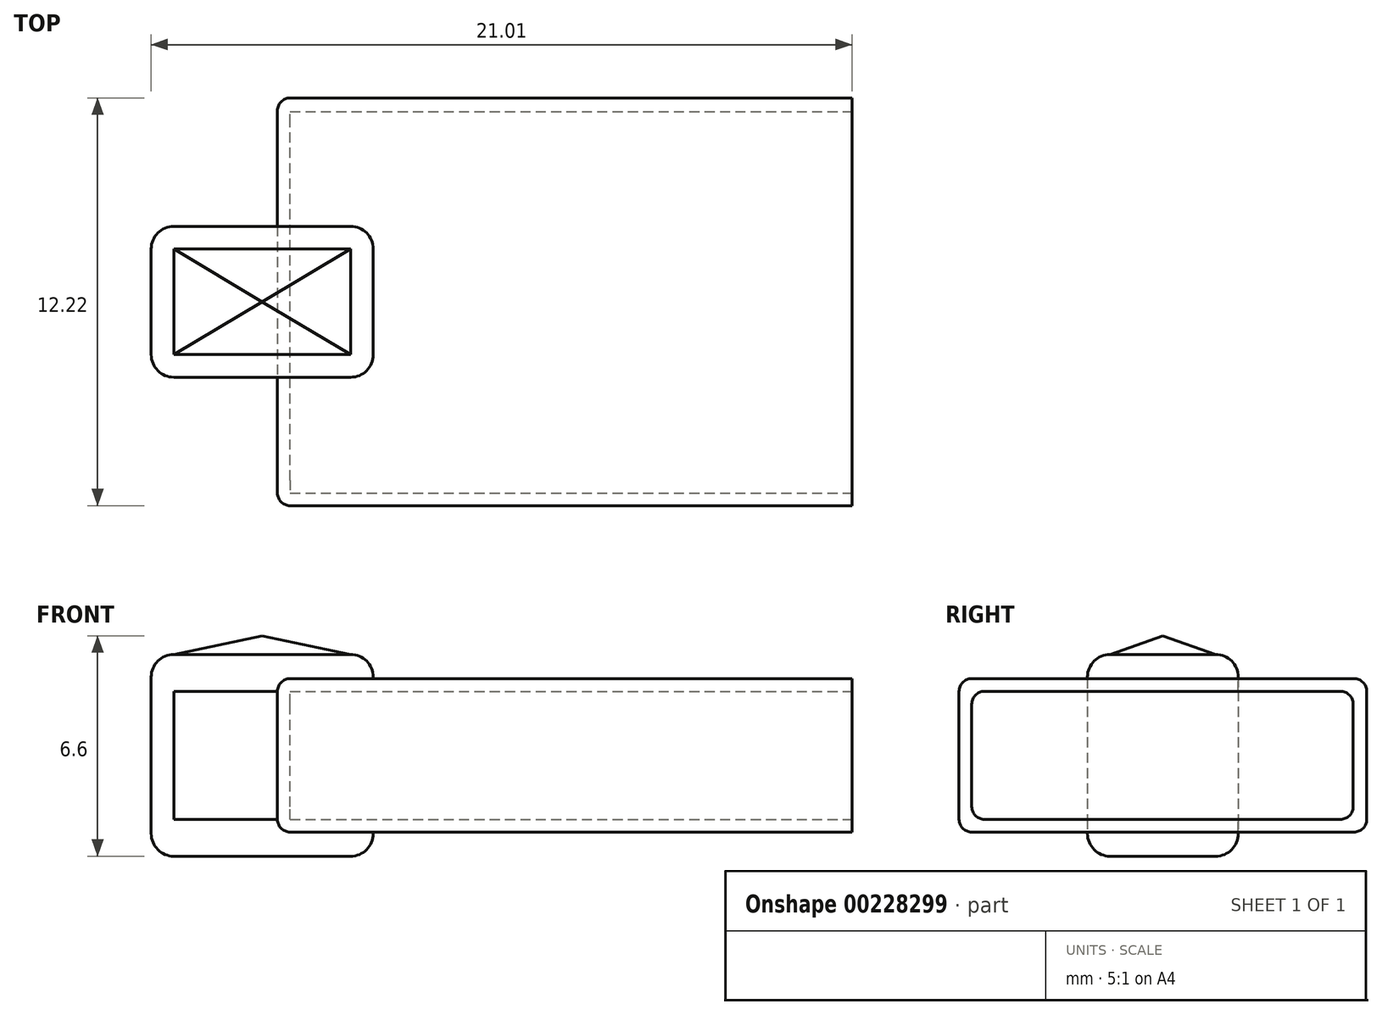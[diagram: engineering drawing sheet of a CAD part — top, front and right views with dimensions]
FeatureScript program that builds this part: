
annotation { "Feature Type Name" : "Feature", "Feature Type Description" : "" }
export const myFeature = defineFeature(function(context is Context, id is Id, definition is map)
    precondition{}
    {
        {
            var Q0;
            Q0=qCreatedBy(makeId("Top.planeOp"),FACE);
            var sketch = newSketch(context, id + "F0", { "sketchPlane" : qUnion([Q0])});
            skLineSegment(sketch, "E0", {"start": v(-8.61, -6.1) * mm, "end": v(-8.61, 6.1) * mm});
            skLineSegment(sketch, "E1", {"start": v(-8.61, 6.1) * mm, "end": v(8.61, 6.1) * mm});
            skLineSegment(sketch, "E2", {"start": v(8.61, 6.1) * mm, "end": v(8.61, -6.1) * mm});
            skLineSegment(sketch, "E3", {"start": v(8.61, -6.1) * mm, "end": v(-8.61, -6.1) * mm});
            skSolve(sketch);
        }
        {
            var Q0;
            Q0=qCreatedBy(makeId("Top.planeOp"),FACE);
            var sketch = newSketch(context, id + "F1", { "sketchPlane" : qUnion([Q0])});
            skLineSegment(sketch, "E4", {"start": v(-12.4, 2.26) * mm, "end": v(-5.74, 2.26) * mm});
            skLineSegment(sketch, "E5", {"start": v(-5.74, 2.26) * mm, "end": v(-5.74, -2.26) * mm});
            skLineSegment(sketch, "E6", {"start": v(-5.74, -2.26) * mm, "end": v(-12.4, -2.26) * mm});
            skLineSegment(sketch, "E7", {"start": v(-12.4, -2.26) * mm, "end": v(-12.4, 2.26) * mm});
            skSolve(sketch);
        }
        {
            var Q0;
            Q0 = qSketchRegion(id + "F0", true);
            extrude(context, id + "F2", {"entities" : qUnion([Q0]), "endBound" : BoundingType.SYMMETRIC, "depth" : 4.6 * mm});
        }
        {
            var Q0;
            Q0=makeQuery(id+"F1.imprint","IMPRINT",FACE,{"disambiguationData":[TD([[makeQuery(id+"F1.imprint","IMPRINT",EDGE,{"derivedFrom":sQuery(id+"F1.wireOp",EDGE,"E4")}),-1.0]])]});
            extrude(context, id + "F3", {"entities" : qUnion([Q0]), "operationType" : NewBodyOperationType.ADD, "endBound" : BoundingType.SYMMETRIC, "depth" : 6.05 * mm});
        }
        {
            var Q0;
            Q0=makeQuery(id+"F3.opExtrude","CAP_EDGE",EDGE,{"disambiguationData":[OSD([sQuery(id+"F1.wireOp",EDGE,"E4")])],"isStart":false});
            var Q1;
            Q1=makeQuery(id+"F3.opExtrude","CAP_EDGE",EDGE,{"disambiguationData":[OSD([sQuery(id+"F1.wireOp",EDGE,"E4")])],"isStart":true});
            var Q2;
            Q2=makeQuery(id+"F3.opExtrude","CAP_EDGE",EDGE,{"disambiguationData":[OSD([sQuery(id+"F1.wireOp",EDGE,"E6")])],"isStart":false});
            var Q3;
            Q3=makeQuery(id+"F3.opExtrude","CAP_EDGE",EDGE,{"disambiguationData":[OSD([sQuery(id+"F1.wireOp",EDGE,"E6")])],"isStart":true});
            var Q4;
            Q4=makeQuery(id+"F3.opExtrude","CAP_EDGE",EDGE,{"disambiguationData":[OSD([sQuery(id+"F1.wireOp",EDGE,"E5")])],"isStart":true});
            var Q5;
            Q5=makeQuery(id+"F3.opExtrude","CAP_EDGE",EDGE,{"disambiguationData":[OSD([sQuery(id+"F1.wireOp",EDGE,"E5")])],"isStart":false});
            var Q6;
            Q6=makeQuery(id+"F3.opExtrude","SWEPT_EDGE",EDGE,{"disambiguationData":[OSD([sQuery(id+"F1.wireOp",EDGE,"E6"),sQuery(id+"F1.wireOp",EDGE,"E7")])]});
            var Q7;
            Q7=makeQuery(id+"F3.opExtrude","SWEPT_EDGE",EDGE,{"disambiguationData":[OSD([sQuery(id+"F1.wireOp",EDGE,"E4"),sQuery(id+"F1.wireOp",EDGE,"E7")])]});
            var Q8;
            Q8=makeQuery(id+"F3.opExtrude","CAP_EDGE",EDGE,{"disambiguationData":[OSD([sQuery(id+"F1.wireOp",EDGE,"E7")])],"isStart":true});
            var Q9;
            Q9=makeQuery(id+"F3.opExtrude","CAP_EDGE",EDGE,{"disambiguationData":[OSD([sQuery(id+"F1.wireOp",EDGE,"E7")])],"isStart":false});
            var Q10;
            {var subQ0=sQuery(id+"F1.wireOp",EDGE,"E4");var subQ1=sQuery(id+"F1.wireOp",EDGE,"E5");Q10=makeQuery(id+"F3.boolean.opBoolean","SPLIT",EDGE,{"disambiguationData":[TD([makeQuery(id+"F2.opExtrude","CAP_FACE",FACE,{"disambiguationData":[OSD([sQuery(id+"F0.wireOp",EDGE,"E0"),sQuery(id+"F0.wireOp",EDGE,"E1"),sQuery(id+"F0.wireOp",EDGE,"E2"),sQuery(id+"F0.wireOp",EDGE,"E3")])],"isStart":true})])],"derivedFrom":makeQuery(id+"F3.opExtrude","SWEPT_EDGE",EDGE,{"disambiguationData":[OSD([subQ0,subQ1])]})});}
            var Q11;
            {var subQ0=sQuery(id+"F1.wireOp",EDGE,"E6");var subQ1=sQuery(id+"F1.wireOp",EDGE,"E5");Q11=makeQuery(id+"F3.boolean.opBoolean","SPLIT",EDGE,{"disambiguationData":[TD([makeQuery(id+"F2.opExtrude","CAP_FACE",FACE,{"disambiguationData":[OSD([sQuery(id+"F0.wireOp",EDGE,"E0"),sQuery(id+"F0.wireOp",EDGE,"E1"),sQuery(id+"F0.wireOp",EDGE,"E2"),sQuery(id+"F0.wireOp",EDGE,"E3")])],"isStart":true})])],"derivedFrom":makeQuery(id+"F3.opExtrude","SWEPT_EDGE",EDGE,{"disambiguationData":[OSD([subQ1,subQ0])]})});}
            var Q12;
            {var subQ0=sQuery(id+"F1.wireOp",EDGE,"E4");var subQ1=sQuery(id+"F1.wireOp",EDGE,"E5");Q12=makeQuery(id+"F3.boolean.opBoolean","SPLIT",EDGE,{"disambiguationData":[TD([makeQuery(id+"F2.opExtrude","CAP_FACE",FACE,{"disambiguationData":[OSD([sQuery(id+"F0.wireOp",EDGE,"E0"),sQuery(id+"F0.wireOp",EDGE,"E1"),sQuery(id+"F0.wireOp",EDGE,"E2"),sQuery(id+"F0.wireOp",EDGE,"E3")])],"isStart":false})])],"derivedFrom":makeQuery(id+"F3.opExtrude","SWEPT_EDGE",EDGE,{"disambiguationData":[OSD([subQ0,subQ1])]})});}
            var Q13;
            {var subQ0=sQuery(id+"F1.wireOp",EDGE,"E6");var subQ1=sQuery(id+"F1.wireOp",EDGE,"E5");Q13=makeQuery(id+"F3.boolean.opBoolean","SPLIT",EDGE,{"disambiguationData":[TD([makeQuery(id+"F2.opExtrude","CAP_FACE",FACE,{"disambiguationData":[OSD([sQuery(id+"F0.wireOp",EDGE,"E0"),sQuery(id+"F0.wireOp",EDGE,"E1"),sQuery(id+"F0.wireOp",EDGE,"E2"),sQuery(id+"F0.wireOp",EDGE,"E3")])],"isStart":false})])],"derivedFrom":makeQuery(id+"F3.opExtrude","SWEPT_EDGE",EDGE,{"disambiguationData":[OSD([subQ1,subQ0])]})});}
            fillet(context, id + "F4", {"entities" : qUnion([Q0, Q1, Q2, Q3, Q4, Q5, Q6, Q7, Q8, Q9, Q10, Q11, Q12, Q13]), "radius" : 0.68 * mm, "tangentPropagation" : true, "allowEdgeOverflow" : false});
        }
        {
            var Q0;
            Q0=makeQuery(id+"F2.opExtrude","CAP_EDGE",EDGE,{"disambiguationData":[OSD([sQuery(id+"F0.wireOp",EDGE,"E1")])],"isStart":false});
            var Q1;
            Q1=makeQuery(id+"F2.opExtrude","CAP_EDGE",EDGE,{"disambiguationData":[OSD([sQuery(id+"F0.wireOp",EDGE,"E1")])],"isStart":true});
            var Q2;
            Q2=makeQuery(id+"F2.opExtrude","SWEPT_EDGE",EDGE,{"disambiguationData":[OSD([sQuery(id+"F0.wireOp",EDGE,"E0"),sQuery(id+"F0.wireOp",EDGE,"E1")])]});
            var Q3;
            {var subQ0=sQuery(id+"F0.wireOp",EDGE,"E0");var subQ1=sQuery(id+"F0.wireOp",EDGE,"E1");Q3=makeQuery(id+"F3.boolean.opBoolean","SPLIT",EDGE,{"disambiguationData":[TD([makeQuery(id+"F2.opExtrude","SWEPT_FACE",FACE,{"disambiguationData":[OSD([subQ1])]})])],"derivedFrom":makeQuery(id+"F2.opExtrude","CAP_EDGE",EDGE,{"disambiguationData":[OSD([subQ0])],"isStart":false})});}
            var Q4;
            {var subQ0=sQuery(id+"F0.wireOp",EDGE,"E0");var subQ1=sQuery(id+"F0.wireOp",EDGE,"E1");Q4=makeQuery(id+"F3.boolean.opBoolean","SPLIT",EDGE,{"disambiguationData":[TD([makeQuery(id+"F2.opExtrude","SWEPT_FACE",FACE,{"disambiguationData":[OSD([subQ1])]})])],"derivedFrom":makeQuery(id+"F2.opExtrude","CAP_EDGE",EDGE,{"disambiguationData":[OSD([subQ0])],"isStart":true})});}
            var Q5;
            {var subQ0=sQuery(id+"F0.wireOp",EDGE,"E0");var subQ1=sQuery(id+"F0.wireOp",EDGE,"E3");Q5=makeQuery(id+"F3.boolean.opBoolean","SPLIT",EDGE,{"disambiguationData":[TD([makeQuery(id+"F2.opExtrude","SWEPT_FACE",FACE,{"disambiguationData":[OSD([subQ1])]})])],"derivedFrom":makeQuery(id+"F2.opExtrude","CAP_EDGE",EDGE,{"disambiguationData":[OSD([subQ0])],"isStart":false})});}
            var Q6;
            {var subQ0=sQuery(id+"F0.wireOp",EDGE,"E0");var subQ1=sQuery(id+"F0.wireOp",EDGE,"E3");Q6=makeQuery(id+"F3.boolean.opBoolean","SPLIT",EDGE,{"disambiguationData":[TD([makeQuery(id+"F2.opExtrude","SWEPT_FACE",FACE,{"disambiguationData":[OSD([subQ1])]})])],"derivedFrom":makeQuery(id+"F2.opExtrude","CAP_EDGE",EDGE,{"disambiguationData":[OSD([subQ0])],"isStart":true})});}
            var Q7;
            Q7=makeQuery(id+"F2.opExtrude","SWEPT_EDGE",EDGE,{"disambiguationData":[OSD([sQuery(id+"F0.wireOp",EDGE,"E0"),sQuery(id+"F0.wireOp",EDGE,"E3")])]});
            var Q8;
            Q8=makeQuery(id+"F2.opExtrude","CAP_EDGE",EDGE,{"disambiguationData":[OSD([sQuery(id+"F0.wireOp",EDGE,"E3")])],"isStart":false});
            var Q9;
            Q9=makeQuery(id+"F2.opExtrude","CAP_EDGE",EDGE,{"disambiguationData":[OSD([sQuery(id+"F0.wireOp",EDGE,"E3")])],"isStart":true});
            fillet(context, id + "F5", {"entities" : qUnion([Q0, Q1, Q2, Q3, Q4, Q5, Q6, Q7, Q8, Q9]), "radius" : 0.38 * mm, "tangentPropagation" : true, "allowEdgeOverflow" : false});
        }
        {
            var Q0;
            Q0=qCreatedBy(makeId("Front.planeOp"),FACE);
            var sketch = newSketch(context, id + "F6", { "sketchPlane" : qUnion([Q0])});
            skLineSegment(sketch, "E8", {"start": v(-9.07, 0) * mm, "end": v(-9.07, 3.58) * mm});
            skSolve(sketch);
        }
        {
            var Q1;
            Q1=makeQuery(id+"F3.opExtrude","CAP_FACE",FACE,{"disambiguationData":[OSD([sQuery(id+"F1.wireOp",EDGE,"E4"),sQuery(id+"F1.wireOp",EDGE,"E5"),sQuery(id+"F1.wireOp",EDGE,"E6"),sQuery(id+"F1.wireOp",EDGE,"E7")])],"isStart":false});
            var Q2;
            Q2=sQuery(id+"F6.wireOp",VERTEX,"E8.end");
            loft(context, id + "F7", {"operationType" : NewBodyOperationType.ADD, "sheetProfilesArray" : [{ "sheetProfileEntities" : qUnion([Q1]) }, { "sheetProfileEntities" : qUnion([Q2]) }]});
        }
        {
            var Q0;
            Q0=makeQuery(id+"F3.opExtrude","SWEPT_FACE",FACE,{"disambiguationData":[OSD([sQuery(id+"F1.wireOp",EDGE,"E6")])]});
            var sketch = newSketch(context, id + "F8", { "sketchPlane" : qUnion([Q0])});
            skLineSegment(sketch, "E9", {"start": v(-8.61, 1.92) * mm, "end": v(-11.72, 1.92) * mm});
            skLineSegment(sketch, "E10", {"start": v(-11.72, 1.92) * mm, "end": v(-11.72, -1.92) * mm});
            skLineSegment(sketch, "E11", {"start": v(-11.72, -1.92) * mm, "end": v(-8.61, -1.92) * mm});
            skLineSegment(sketch, "E12", {"start": v(-8.61, -1.92) * mm, "end": v(-8.61, 1.92) * mm});
            skSolve(sketch);
        }
        {
            var Q0;
            Q0=makeQuery(id+"F8.imprint","IMPRINT",FACE,{"disambiguationData":[TD([[makeQuery(id+"F8.imprint","IMPRINT",EDGE,{"derivedFrom":sQuery(id+"F8.wireOp",EDGE,"E9")}),1.0]])]});
            extrude(context, id + "F9", {"entities" : qUnion([Q0]), "operationType" : NewBodyOperationType.REMOVE, "oppositeDirection" : true, "depth" : 4.52 * mm});
        }
        {
            var Q0;
            Q0=makeQuery(id+"F2.opExtrude","SWEPT_FACE",FACE,{"disambiguationData":[OSD([sQuery(id+"F0.wireOp",EDGE,"E2")])]});
            var sketch = newSketch(context, id + "F10", { "sketchPlane" : qUnion([Q0])});
            skLineSegment(sketch, "E13", {"start": v(0, 1.92) * mm, "end": v(5.7, 1.92) * mm});
            skLineSegment(sketch, "E14", {"start": v(5.7, 1.92) * mm, "end": v(5.7, -1.92) * mm});
            skLineSegment(sketch, "E15", {"start": v(5.7, -1.92) * mm, "end": v(0, -1.92) * mm});
            skLineSegment(sketch, "E16", {"start": v(0, -1.92) * mm, "end": v(-5.73, -1.92) * mm});
            skLineSegment(sketch, "E17", {"start": v(-5.73, -1.92) * mm, "end": v(-5.73, 0) * mm});
            skLineSegment(sketch, "E18", {"start": v(-5.73, 0) * mm, "end": v(-5.73, 1.92) * mm});
            skLineSegment(sketch, "E19", {"start": v(-5.73, 1.92) * mm, "end": v(0, 1.92) * mm});
            skSolve(sketch);
        }
        {
            var Q0;
            Q0=makeQuery(id+"F10.imprint","IMPRINT",FACE,{"disambiguationData":[TD([[makeQuery(id+"F10.imprint","IMPRINT",EDGE,{"derivedFrom":sQuery(id+"F10.wireOp",EDGE,"E13")}),-1.0]])]});
            extrude(context, id + "F11", {"entities" : qUnion([Q0]), "operationType" : NewBodyOperationType.REMOVE, "oppositeDirection" : true, "depth" : 16.84 * mm});
        }
        {
            var Q0;
            Q0=makeQuery(id+"F11.boolean.opBoolean","COPY",EDGE,{"derivedFrom":makeQuery(id+"F11.opExtrude","SWEPT_EDGE",EDGE,{"disambiguationData":[OSD([sQuery(id+"F10.wireOp",EDGE,"E13"),sQuery(id+"F10.wireOp",EDGE,"E14")])]})});
            var Q1;
            Q1=makeQuery(id+"F11.boolean.opBoolean","COPY",EDGE,{"derivedFrom":makeQuery(id+"F11.opExtrude","SWEPT_EDGE",EDGE,{"disambiguationData":[OSD([sQuery(id+"F10.wireOp",EDGE,"E18"),sQuery(id+"F10.wireOp",EDGE,"E19")])]})});
            var Q2;
            Q2=makeQuery(id+"F11.boolean.opBoolean","COPY",EDGE,{"derivedFrom":makeQuery(id+"F11.opExtrude","SWEPT_EDGE",EDGE,{"disambiguationData":[OSD([sQuery(id+"F10.wireOp",EDGE,"E16"),sQuery(id+"F10.wireOp",EDGE,"E17")])]})});
            var Q3;
            Q3=makeQuery(id+"F11.boolean.opBoolean","COPY",EDGE,{"derivedFrom":makeQuery(id+"F11.opExtrude","SWEPT_EDGE",EDGE,{"disambiguationData":[OSD([sQuery(id+"F10.wireOp",EDGE,"E14"),sQuery(id+"F10.wireOp",EDGE,"E15")])]})});
            fillet(context, id + "F12", {"entities" : qUnion([Q0, Q1, Q2, Q3]), "radius" : 0.38 * mm, "tangentPropagation" : true, "allowEdgeOverflow" : false});
        }
    });
